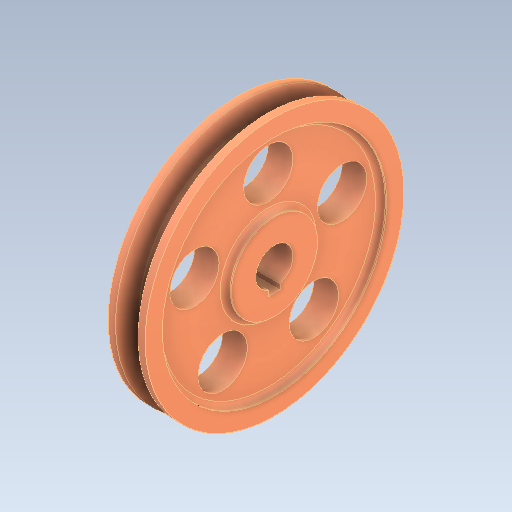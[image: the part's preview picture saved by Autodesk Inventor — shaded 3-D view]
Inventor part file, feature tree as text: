
AUTODESK INVENTOR PART (.ipt)
format: ipt  version: 2021 (Build 250183000, 183)  size: 236,544 bytes
history: mixed  units: mm
features: other x1, extrude x1, imported_body x1
ambient origin geometry x8: Origin, YZ Plane, XZ Plane, XY Plane, X Axis, Y Axis, Z Axis, Center Point
bodies: Body1 (imported_parasolid)
feature tree (3):
  other  "Sólido1"
  extrude  "Extrude2"  [1 undecoded]
  imported_body  NMx_Import_Brep_tag  [imported B-rep: ~28 faces, bbox_mm=[15.0, 62.861888, 79.36811]]
note: 1 required parameter value undecoded (feature->parameter linkage not recoverable at this tier; creation-order binding heuristic only, values carry confidence <= 0.55)
